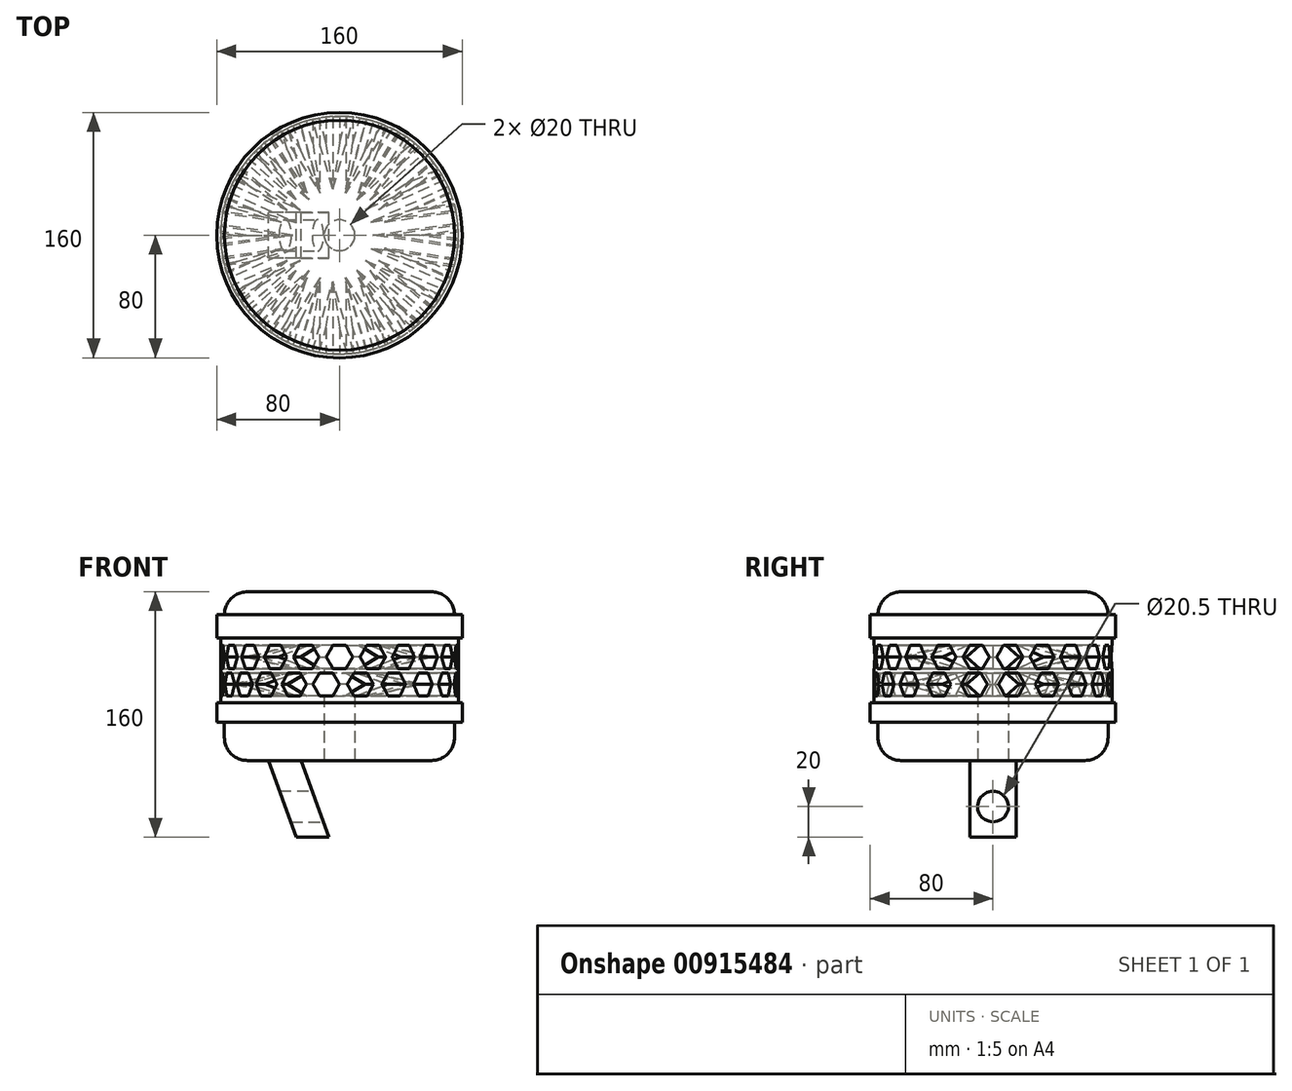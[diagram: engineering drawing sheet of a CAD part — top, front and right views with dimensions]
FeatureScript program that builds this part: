
annotation { "Feature Type Name" : "Feature", "Feature Type Description" : "" }
export const myFeature = defineFeature(function(context is Context, id is Id, definition is map)
    precondition{}
    {
        {
            var Q0;
            Q0=qCreatedBy(makeId("Top.planeOp"),FACE);
            var sketch = newSketch(context, id + "F0", { "sketchPlane" : qUnion([Q0])});
            skCircle(sketch, "E0", {"center": v(0, 0) * mm, "radius": 75 * mm});
            skCircle(sketch, "E1", {"center": v(0, 0) * mm, "radius": 80 * mm});
            skCircle(sketch, "E2", {"center": v(0, 0) * mm, "radius": 77.5 * mm});
            skSolve(sketch);
        }
        {
            var Q0;
            Q0=makeQuery(id+"F0.imprint","IMPRINT",FACE,{"disambiguationData":[TD([[makeQuery(id+"F0.imprint","IMPRINT",EDGE,{"derivedFrom":sQuery(id+"F0.wireOp",EDGE,"E0")}),1.0]])]});
            extrude(context, id + "F1", {"entities" : qUnion([Q0]), "depth" : 110 * mm, "offsetDistance" : 25 * mm});
        }
        {
            var Q0;
            Q0=makeQuery(id+"F1.opExtrude","CAP_EDGE",EDGE,{"disambiguationData":[OSD([sQuery(id+"F0.wireOp",EDGE,"E0")])],"isStart":false});
            var Q1;
            Q1=makeQuery(id+"F1.opExtrude","CAP_EDGE",EDGE,{"disambiguationData":[OSD([sQuery(id+"F0.wireOp",EDGE,"E0")])],"isStart":true});
            fillet(context, id + "F2", {"entities" : qUnion([Q0, Q1]), "radius" : 15 * mm, "tangentPropagation" : true, "allowEdgeOverflow" : false});
        }
        {
            var Q0;
            Q0=makeQuery(id+"F0.imprint","IMPRINT",FACE,{"disambiguationData":[TD([[makeQuery(id+"F0.imprint","IMPRINT",EDGE,{"derivedFrom":sQuery(id+"F0.wireOp",EDGE,"E0")}),-1.0]])]});
            var Q1;
            Q1=makeQuery(id+"F0.imprint","IMPRINT",FACE,{"disambiguationData":[TD([[makeQuery(id+"F0.imprint","IMPRINT",EDGE,{"derivedFrom":sQuery(id+"F0.wireOp",EDGE,"E1")}),1.0]])]});
            extrude(context, id + "F3", {"entities" : qUnion([Q0, Q1]), "operationType" : NewBodyOperationType.ADD, "depth" : 95 * mm, "offsetDistance" : 25 * mm});
        }
        {
            var Q0;
            Q0=makeQuery(id+"F0.imprint","IMPRINT",FACE,{"disambiguationData":[TD([[makeQuery(id+"F0.imprint","IMPRINT",EDGE,{"derivedFrom":sQuery(id+"F0.wireOp",EDGE,"E1")}),1.0]])]});
            extrude(context, id + "F4", {"entities" : qUnion([Q0]), "operationType" : NewBodyOperationType.REMOVE, "depth" : 80 * mm, "offsetDistance" : 25 * mm});
        }
        {
            var Q0;
            Q0=makeQuery(id+"F0.imprint","IMPRINT",FACE,{"disambiguationData":[TD([[makeQuery(id+"F0.imprint","IMPRINT",EDGE,{"derivedFrom":sQuery(id+"F0.wireOp",EDGE,"E1")}),1.0]])]});
            extrude(context, id + "F5", {"entities" : qUnion([Q0]), "operationType" : NewBodyOperationType.ADD, "depth" : 37.5 * mm, "offsetDistance" : 25 * mm});
        }
        {
            var Q0;
            Q0=makeQuery(id+"F0.imprint","IMPRINT",FACE,{"disambiguationData":[TD([[makeQuery(id+"F0.imprint","IMPRINT",EDGE,{"derivedFrom":sQuery(id+"F0.wireOp",EDGE,"E1")}),1.0]])]});
            var Q1;
            Q1=makeQuery(id+"F0.imprint","IMPRINT",FACE,{"disambiguationData":[TD([[makeQuery(id+"F0.imprint","IMPRINT",EDGE,{"derivedFrom":sQuery(id+"F0.wireOp",EDGE,"E0")}),-1.0]])]});
            extrude(context, id + "F6", {"entities" : qUnion([Q0, Q1]), "operationType" : NewBodyOperationType.REMOVE, "depth" : 25 * mm, "offsetDistance" : 25 * mm});
        }
        {
            var Q0;
            Q0=qCreatedBy(makeId("Front.planeOp"),FACE);
            var sketch = newSketch(context, id + "F7", { "sketchPlane" : qUnion([Q0])});
            skCircle(sketch, "E3.cCircle", {"center": v(0, 67.5) * mm, "radius": 8.66 * mm, "construction": true});
            skLineSegment(sketch, "E3.0", {"start": v(4.33, 75) * mm, "end": v(8.66, 67.5) * mm});
            skLineSegment(sketch, "E3.1", {"start": v(8.66, 67.5) * mm, "end": v(4.33, 60) * mm});
            skLineSegment(sketch, "E3.2", {"start": v(4.33, 60) * mm, "end": v(-4.33, 60) * mm});
            skLineSegment(sketch, "E3.3", {"start": v(-4.33, 60) * mm, "end": v(-8.66, 67.5) * mm});
            skLineSegment(sketch, "E3.4", {"start": v(-8.66, 67.5) * mm, "end": v(-4.33, 75) * mm});
            skLineSegment(sketch, "E3.5", {"start": v(-4.33, 75) * mm, "end": v(4.33, 75) * mm});
            skLineSegment(sketch, "E4", {"start": v(0, 67.5) * mm, "end": v(-8.66, 67.5) * mm});
            skLineSegment(sketch, "E5", {"start": v(-8.66, 67.5) * mm, "end": v(-8.66, 49.65) * mm});
            skCircle(sketch, "E6.cCircle", {"center": v(-8.66, 49.65) * mm, "radius": 8.66 * mm, "construction": true});
            skLineSegment(sketch, "E6.0", {"start": v(-13, 57.15) * mm, "end": v(-4.33, 57.15) * mm});
            skLineSegment(sketch, "E6.1", {"start": v(-4.33, 57.15) * mm, "end": v(0, 49.65) * mm});
            skLineSegment(sketch, "E6.2", {"start": v(0, 49.65) * mm, "end": v(-4.33, 42.15) * mm});
            skLineSegment(sketch, "E6.3", {"start": v(-4.33, 42.15) * mm, "end": v(-13, 42.15) * mm});
            skLineSegment(sketch, "E6.4", {"start": v(-13, 42.15) * mm, "end": v(-17.32, 49.65) * mm});
            skLineSegment(sketch, "E6.5", {"start": v(-17.32, 49.65) * mm, "end": v(-13, 57.15) * mm});
            skSolve(sketch);
        }
        {
            var Q0;
            Q0=makeQuery(id+"F7.imprint","IMPRINT",FACE,{"disambiguationData":[TD([[makeQuery(id+"F7.imprint","IMPRINT",EDGE,{"derivedFrom":sQuery(id+"F7.wireOp",EDGE,"E3.0")}),-1.0]])]});
            var Q1;
            {var subQ0=sQuery(id+"F7.wireOp",EDGE,"E6.1");Q1=makeQuery(id+"F7.imprint","IMPRINT",FACE,{"disambiguationData":[TD([[makeQuery(id+"F7.imprint","IMPRINT",EDGE,{"derivedFrom":subQ0}),-1.0]])]});}
            extrude(context, id + "F8", {"entities" : qUnion([Q0, Q1]), "oppositeDirection" : true, "depth" : 120 * mm, "offsetDistance" : 25 * mm, "hasSecondDirection" : true, "secondDirectionOppositeDirection" : false, "secondDirectionDepth" : 120 * mm});
        }
        {
            var Q0;
            Q0=qCreatedBy(makeId("Right.planeOp"),FACE);
            var sketch = newSketch(context, id + "F9", { "sketchPlane" : qUnion([Q0])});
            skLineSegment(sketch, "E7", {"start": v(0, 0) * mm, "end": v(0, 75) * mm});
            skSolve(sketch);
        }
        {
            var Q0;
            Q0=makeQuery(id+"F8.opExtrude","SWEPT_BODY",BODY,{"disambiguationData":[OSD([sQuery(id+"F7.wireOp",EDGE,"E3.0"),sQuery(id+"F7.wireOp",EDGE,"E3.1"),sQuery(id+"F7.wireOp",EDGE,"E3.2"),sQuery(id+"F7.wireOp",EDGE,"E3.3"),sQuery(id+"F7.wireOp",EDGE,"E3.4"),sQuery(id+"F7.wireOp",EDGE,"E3.5")])]});
            var Q1;
            Q1=sQuery(id+"F9.wireOp",EDGE,"E7");
            circularPattern(context, id + "F10", {"entities" : qUnion([Q0]), "axis" : qUnion([Q1]), "angle" : 360 * degree, "instanceCount" : 11, "equalSpace" : true});
        }
        {
            var Q0;
            Q0=qCreatedBy(makeId("Front.planeOp"),FACE);
            var sketch = newSketch(context, id + "F11", { "sketchPlane" : qUnion([Q0])});
            skLineSegment(sketch, "E8", {"start": v(-8.66, 0) * mm, "end": v(-8.66, 49.45) * mm});
            skSolve(sketch);
        }
        {
            var Q0;
            Q0=makeQuery(id+"F8.opExtrude","SWEPT_BODY",BODY,{"disambiguationData":[OSD([sQuery(id+"F7.wireOp",EDGE,"E6.0"),sQuery(id+"F7.wireOp",EDGE,"E6.1"),sQuery(id+"F7.wireOp",EDGE,"E6.2"),sQuery(id+"F7.wireOp",EDGE,"E6.3"),sQuery(id+"F7.wireOp",EDGE,"E6.4"),sQuery(id+"F7.wireOp",EDGE,"E6.5")])]});
            var Q1;
            Q1=sQuery(id+"F11.wireOp",EDGE,"E8");
            circularPattern(context, id + "F12", {"entities" : qUnion([Q0]), "axis" : qUnion([Q1]), "angle" : 360 * degree, "instanceCount" : 11, "equalSpace" : true});
        }
        {
            var Q0;
            Q0=makeQuery(id+"F8.opExtrude","SWEPT_BODY",BODY,{"disambiguationData":[OSD([sQuery(id+"F7.wireOp",EDGE,"E3.0"),sQuery(id+"F7.wireOp",EDGE,"E3.1"),sQuery(id+"F7.wireOp",EDGE,"E3.2"),sQuery(id+"F7.wireOp",EDGE,"E3.3"),sQuery(id+"F7.wireOp",EDGE,"E3.4"),sQuery(id+"F7.wireOp",EDGE,"E3.5")])]});
            var Q1;
            Q1=makeQuery(id+"F10.opPattern","COPY",BODY,{"derivedFrom":makeQuery(id+"F8.opExtrude","SWEPT_BODY",BODY,{"disambiguationData":[OSD([sQuery(id+"F7.wireOp",EDGE,"E3.0"),sQuery(id+"F7.wireOp",EDGE,"E3.1"),sQuery(id+"F7.wireOp",EDGE,"E3.2"),sQuery(id+"F7.wireOp",EDGE,"E3.3"),sQuery(id+"F7.wireOp",EDGE,"E3.4"),sQuery(id+"F7.wireOp",EDGE,"E3.5")])]}),"instanceName":"5"});
            var Q2;
            Q2=makeQuery(id+"F10.opPattern","COPY",BODY,{"derivedFrom":makeQuery(id+"F8.opExtrude","SWEPT_BODY",BODY,{"disambiguationData":[OSD([sQuery(id+"F7.wireOp",EDGE,"E3.0"),sQuery(id+"F7.wireOp",EDGE,"E3.1"),sQuery(id+"F7.wireOp",EDGE,"E3.2"),sQuery(id+"F7.wireOp",EDGE,"E3.3"),sQuery(id+"F7.wireOp",EDGE,"E3.4"),sQuery(id+"F7.wireOp",EDGE,"E3.5")])]}),"instanceName":"6"});
            var Q3;
            Q3=makeQuery(id+"F10.opPattern","COPY",BODY,{"derivedFrom":makeQuery(id+"F8.opExtrude","SWEPT_BODY",BODY,{"disambiguationData":[OSD([sQuery(id+"F7.wireOp",EDGE,"E3.0"),sQuery(id+"F7.wireOp",EDGE,"E3.1"),sQuery(id+"F7.wireOp",EDGE,"E3.2"),sQuery(id+"F7.wireOp",EDGE,"E3.3"),sQuery(id+"F7.wireOp",EDGE,"E3.4"),sQuery(id+"F7.wireOp",EDGE,"E3.5")])]}),"instanceName":"1"});
            var Q4;
            Q4=makeQuery(id+"F10.opPattern","COPY",BODY,{"derivedFrom":makeQuery(id+"F8.opExtrude","SWEPT_BODY",BODY,{"disambiguationData":[OSD([sQuery(id+"F7.wireOp",EDGE,"E3.0"),sQuery(id+"F7.wireOp",EDGE,"E3.1"),sQuery(id+"F7.wireOp",EDGE,"E3.2"),sQuery(id+"F7.wireOp",EDGE,"E3.3"),sQuery(id+"F7.wireOp",EDGE,"E3.4"),sQuery(id+"F7.wireOp",EDGE,"E3.5")])]}),"instanceName":"7"});
            var Q5;
            Q5=makeQuery(id+"F10.opPattern","COPY",BODY,{"derivedFrom":makeQuery(id+"F8.opExtrude","SWEPT_BODY",BODY,{"disambiguationData":[OSD([sQuery(id+"F7.wireOp",EDGE,"E3.0"),sQuery(id+"F7.wireOp",EDGE,"E3.1"),sQuery(id+"F7.wireOp",EDGE,"E3.2"),sQuery(id+"F7.wireOp",EDGE,"E3.3"),sQuery(id+"F7.wireOp",EDGE,"E3.4"),sQuery(id+"F7.wireOp",EDGE,"E3.5")])]}),"instanceName":"2"});
            var Q6;
            Q6=makeQuery(id+"F10.opPattern","COPY",BODY,{"derivedFrom":makeQuery(id+"F8.opExtrude","SWEPT_BODY",BODY,{"disambiguationData":[OSD([sQuery(id+"F7.wireOp",EDGE,"E3.0"),sQuery(id+"F7.wireOp",EDGE,"E3.1"),sQuery(id+"F7.wireOp",EDGE,"E3.2"),sQuery(id+"F7.wireOp",EDGE,"E3.3"),sQuery(id+"F7.wireOp",EDGE,"E3.4"),sQuery(id+"F7.wireOp",EDGE,"E3.5")])]}),"instanceName":"8"});
            var Q7;
            Q7=makeQuery(id+"F10.opPattern","COPY",BODY,{"derivedFrom":makeQuery(id+"F8.opExtrude","SWEPT_BODY",BODY,{"disambiguationData":[OSD([sQuery(id+"F7.wireOp",EDGE,"E3.0"),sQuery(id+"F7.wireOp",EDGE,"E3.1"),sQuery(id+"F7.wireOp",EDGE,"E3.2"),sQuery(id+"F7.wireOp",EDGE,"E3.3"),sQuery(id+"F7.wireOp",EDGE,"E3.4"),sQuery(id+"F7.wireOp",EDGE,"E3.5")])]}),"instanceName":"3"});
            var Q8;
            Q8=makeQuery(id+"F10.opPattern","COPY",BODY,{"derivedFrom":makeQuery(id+"F8.opExtrude","SWEPT_BODY",BODY,{"disambiguationData":[OSD([sQuery(id+"F7.wireOp",EDGE,"E3.0"),sQuery(id+"F7.wireOp",EDGE,"E3.1"),sQuery(id+"F7.wireOp",EDGE,"E3.2"),sQuery(id+"F7.wireOp",EDGE,"E3.3"),sQuery(id+"F7.wireOp",EDGE,"E3.4"),sQuery(id+"F7.wireOp",EDGE,"E3.5")])]}),"instanceName":"9"});
            var Q9;
            Q9=makeQuery(id+"F10.opPattern","COPY",BODY,{"derivedFrom":makeQuery(id+"F8.opExtrude","SWEPT_BODY",BODY,{"disambiguationData":[OSD([sQuery(id+"F7.wireOp",EDGE,"E3.0"),sQuery(id+"F7.wireOp",EDGE,"E3.1"),sQuery(id+"F7.wireOp",EDGE,"E3.2"),sQuery(id+"F7.wireOp",EDGE,"E3.3"),sQuery(id+"F7.wireOp",EDGE,"E3.4"),sQuery(id+"F7.wireOp",EDGE,"E3.5")])]}),"instanceName":"4"});
            var Q10;
            Q10=makeQuery(id+"F10.opPattern","COPY",BODY,{"derivedFrom":makeQuery(id+"F8.opExtrude","SWEPT_BODY",BODY,{"disambiguationData":[OSD([sQuery(id+"F7.wireOp",EDGE,"E3.0"),sQuery(id+"F7.wireOp",EDGE,"E3.1"),sQuery(id+"F7.wireOp",EDGE,"E3.2"),sQuery(id+"F7.wireOp",EDGE,"E3.3"),sQuery(id+"F7.wireOp",EDGE,"E3.4"),sQuery(id+"F7.wireOp",EDGE,"E3.5")])]}),"instanceName":"10"});
            var Q11;
            Q11=makeQuery(id+"F12.opPattern","COPY",BODY,{"derivedFrom":makeQuery(id+"F8.opExtrude","SWEPT_BODY",BODY,{"disambiguationData":[OSD([sQuery(id+"F7.wireOp",EDGE,"E6.0"),sQuery(id+"F7.wireOp",EDGE,"E6.1"),sQuery(id+"F7.wireOp",EDGE,"E6.2"),sQuery(id+"F7.wireOp",EDGE,"E6.3"),sQuery(id+"F7.wireOp",EDGE,"E6.4"),sQuery(id+"F7.wireOp",EDGE,"E6.5")])]}),"instanceName":"6"});
            var Q12;
            Q12=makeQuery(id+"F12.opPattern","COPY",BODY,{"derivedFrom":makeQuery(id+"F8.opExtrude","SWEPT_BODY",BODY,{"disambiguationData":[OSD([sQuery(id+"F7.wireOp",EDGE,"E6.0"),sQuery(id+"F7.wireOp",EDGE,"E6.1"),sQuery(id+"F7.wireOp",EDGE,"E6.2"),sQuery(id+"F7.wireOp",EDGE,"E6.3"),sQuery(id+"F7.wireOp",EDGE,"E6.4"),sQuery(id+"F7.wireOp",EDGE,"E6.5")])]}),"instanceName":"1"});
            var Q13;
            Q13=makeQuery(id+"F12.opPattern","COPY",BODY,{"derivedFrom":makeQuery(id+"F8.opExtrude","SWEPT_BODY",BODY,{"disambiguationData":[OSD([sQuery(id+"F7.wireOp",EDGE,"E6.0"),sQuery(id+"F7.wireOp",EDGE,"E6.1"),sQuery(id+"F7.wireOp",EDGE,"E6.2"),sQuery(id+"F7.wireOp",EDGE,"E6.3"),sQuery(id+"F7.wireOp",EDGE,"E6.4"),sQuery(id+"F7.wireOp",EDGE,"E6.5")])]}),"instanceName":"5"});
            var Q14;
            Q14=makeQuery(id+"F12.opPattern","COPY",BODY,{"derivedFrom":makeQuery(id+"F8.opExtrude","SWEPT_BODY",BODY,{"disambiguationData":[OSD([sQuery(id+"F7.wireOp",EDGE,"E6.0"),sQuery(id+"F7.wireOp",EDGE,"E6.1"),sQuery(id+"F7.wireOp",EDGE,"E6.2"),sQuery(id+"F7.wireOp",EDGE,"E6.3"),sQuery(id+"F7.wireOp",EDGE,"E6.4"),sQuery(id+"F7.wireOp",EDGE,"E6.5")])]}),"instanceName":"10"});
            var Q15;
            Q15=makeQuery(id+"F12.opPattern","COPY",BODY,{"derivedFrom":makeQuery(id+"F8.opExtrude","SWEPT_BODY",BODY,{"disambiguationData":[OSD([sQuery(id+"F7.wireOp",EDGE,"E6.0"),sQuery(id+"F7.wireOp",EDGE,"E6.1"),sQuery(id+"F7.wireOp",EDGE,"E6.2"),sQuery(id+"F7.wireOp",EDGE,"E6.3"),sQuery(id+"F7.wireOp",EDGE,"E6.4"),sQuery(id+"F7.wireOp",EDGE,"E6.5")])]}),"instanceName":"4"});
            var Q16;
            Q16=makeQuery(id+"F12.opPattern","COPY",BODY,{"derivedFrom":makeQuery(id+"F8.opExtrude","SWEPT_BODY",BODY,{"disambiguationData":[OSD([sQuery(id+"F7.wireOp",EDGE,"E6.0"),sQuery(id+"F7.wireOp",EDGE,"E6.1"),sQuery(id+"F7.wireOp",EDGE,"E6.2"),sQuery(id+"F7.wireOp",EDGE,"E6.3"),sQuery(id+"F7.wireOp",EDGE,"E6.4"),sQuery(id+"F7.wireOp",EDGE,"E6.5")])]}),"instanceName":"9"});
            var Q17;
            Q17=makeQuery(id+"F12.opPattern","COPY",BODY,{"derivedFrom":makeQuery(id+"F8.opExtrude","SWEPT_BODY",BODY,{"disambiguationData":[OSD([sQuery(id+"F7.wireOp",EDGE,"E6.0"),sQuery(id+"F7.wireOp",EDGE,"E6.1"),sQuery(id+"F7.wireOp",EDGE,"E6.2"),sQuery(id+"F7.wireOp",EDGE,"E6.3"),sQuery(id+"F7.wireOp",EDGE,"E6.4"),sQuery(id+"F7.wireOp",EDGE,"E6.5")])]}),"instanceName":"3"});
            var Q18;
            Q18=makeQuery(id+"F12.opPattern","COPY",BODY,{"derivedFrom":makeQuery(id+"F8.opExtrude","SWEPT_BODY",BODY,{"disambiguationData":[OSD([sQuery(id+"F7.wireOp",EDGE,"E6.0"),sQuery(id+"F7.wireOp",EDGE,"E6.1"),sQuery(id+"F7.wireOp",EDGE,"E6.2"),sQuery(id+"F7.wireOp",EDGE,"E6.3"),sQuery(id+"F7.wireOp",EDGE,"E6.4"),sQuery(id+"F7.wireOp",EDGE,"E6.5")])]}),"instanceName":"8"});
            var Q19;
            Q19=makeQuery(id+"F12.opPattern","COPY",BODY,{"derivedFrom":makeQuery(id+"F8.opExtrude","SWEPT_BODY",BODY,{"disambiguationData":[OSD([sQuery(id+"F7.wireOp",EDGE,"E6.0"),sQuery(id+"F7.wireOp",EDGE,"E6.1"),sQuery(id+"F7.wireOp",EDGE,"E6.2"),sQuery(id+"F7.wireOp",EDGE,"E6.3"),sQuery(id+"F7.wireOp",EDGE,"E6.4"),sQuery(id+"F7.wireOp",EDGE,"E6.5")])]}),"instanceName":"2"});
            var Q20;
            Q20=makeQuery(id+"F12.opPattern","COPY",BODY,{"derivedFrom":makeQuery(id+"F8.opExtrude","SWEPT_BODY",BODY,{"disambiguationData":[OSD([sQuery(id+"F7.wireOp",EDGE,"E6.0"),sQuery(id+"F7.wireOp",EDGE,"E6.1"),sQuery(id+"F7.wireOp",EDGE,"E6.2"),sQuery(id+"F7.wireOp",EDGE,"E6.3"),sQuery(id+"F7.wireOp",EDGE,"E6.4"),sQuery(id+"F7.wireOp",EDGE,"E6.5")])]}),"instanceName":"7"});
            var Q21;
            Q21=makeQuery(id+"F8.opExtrude","SWEPT_BODY",BODY,{"disambiguationData":[OSD([sQuery(id+"F7.wireOp",EDGE,"E6.0"),sQuery(id+"F7.wireOp",EDGE,"E6.1"),sQuery(id+"F7.wireOp",EDGE,"E6.2"),sQuery(id+"F7.wireOp",EDGE,"E6.3"),sQuery(id+"F7.wireOp",EDGE,"E6.4"),sQuery(id+"F7.wireOp",EDGE,"E6.5")])]});
            var Q22;
            Q22=makeQuery(id+"F1.opExtrude","SWEPT_BODY",BODY,{"disambiguationData":[OSD([sQuery(id+"F0.wireOp",EDGE,"E0")])]});
            booleanBodies(context, id + "F13", {"operationType" : BooleanOperationType.SUBTRACTION, "tools" : qUnion([Q0, Q1, Q2, Q3, Q4, Q5, Q6, Q7, Q8, Q9, Q10, Q11, Q12, Q13, Q14, Q15, Q16, Q17, Q18, Q19, Q20, Q21]), "targets" : qUnion([Q22])});
        }
        {
            var Q0;
            Q0=makeQuery(id+"F0.imprint","IMPRINT",FACE,{"disambiguationData":[TD([[makeQuery(id+"F0.imprint","IMPRINT",EDGE,{"derivedFrom":sQuery(id+"F0.wireOp",EDGE,"E0")}),1.0]])]});
            var sketch = newSketch(context, id + "F14", { "sketchPlane" : qUnion([Q0])});
            skCircle(sketch, "E9", {"center": v(0, 0) * mm, "radius": 10 * mm});
            skSolve(sketch);
        }
        {
            var Q0;
            Q0=makeQuery(id+"F14.imprint","IMPRINT",FACE,{"disambiguationData":[TD([[makeQuery(id+"F14.imprint","IMPRINT",EDGE,{"derivedFrom":sQuery(id+"F14.wireOp",EDGE,"E9")}),1.0]])]});
            extrude(context, id + "F15", {"entities" : qUnion([Q0]), "operationType" : NewBodyOperationType.REMOVE, "depth" : 61.6 * mm, "offsetDistance" : 25 * mm});
        }
        {
            var Q0;
            Q0=qCreatedBy(makeId("Front.planeOp"),FACE);
            var sketch = newSketch(context, id + "F16", { "sketchPlane" : qUnion([Q0])});
            skLineSegment(sketch, "E10", {"start": v(0, 0) * mm, "end": v(0, -50) * mm});
            skLineSegment(sketch, "E11", {"start": v(0, -50) * mm, "end": v(-25, -50) * mm});
            skLineSegment(sketch, "E12", {"start": v(-25, -50) * mm, "end": v(-25, 0) * mm});
            skLineSegment(sketch, "E13", {"start": v(-25, 0) * mm, "end": v(-6.8, -50) * mm});
            skLineSegment(sketch, "E14", {"start": v(-28.09, -50) * mm, "end": v(-46.28, 0) * mm});
            skLineSegment(sketch, "E15", {"start": v(-6.8, -50) * mm, "end": v(-28.09, -50) * mm});
            skLineSegment(sketch, "E16", {"start": v(-25, 0) * mm, "end": v(-46.28, 0) * mm});
            skSolve(sketch);
        }
        {
            var Q0;
            Q0=makeQuery(id+"F16.imprint","IMPRINT",FACE,{"disambiguationData":[TD([[makeQuery(id+"F16.imprint","IMPRINT",EDGE,{"derivedFrom":sQuery(id+"F16.wireOp",EDGE,"E13")}),-1.0]])]});
            var Q1;
            {var subQ0=sQuery(id+"F16.wireOp",EDGE,"E12");Q1=makeQuery(id+"F16.imprint","IMPRINT",FACE,{"disambiguationData":[TD([[makeQuery(id+"F16.imprint","IMPRINT",EDGE,{"derivedFrom":subQ0}),1.0]])]});}
            extrude(context, id + "F17", {"entities" : qUnion([Q0, Q1]), "operationType" : NewBodyOperationType.ADD, "depth" : 15 * mm, "offsetDistance" : 25 * mm, "hasSecondDirection" : true, "secondDirectionOppositeDirection" : true, "secondDirectionDepth" : 15 * mm});
        }
        {
            var Q0;
            Q0=qCreatedBy(makeId("Right.planeOp"),FACE);
            var sketch = newSketch(context, id + "F18", { "sketchPlane" : qUnion([Q0])});
            skCircle(sketch, "E17", {"center": v(0, -30) * mm, "radius": 10.25 * mm});
            skSolve(sketch);
        }
        {
            var Q0;
            Q0=makeQuery(id+"F18.imprint","IMPRINT",FACE,{"disambiguationData":[TD([[makeQuery(id+"F18.imprint","IMPRINT",EDGE,{"derivedFrom":sQuery(id+"F18.wireOp",EDGE,"E17")}),1.0]])]});
            extrude(context, id + "F19", {"entities" : qUnion([Q0]), "operationType" : NewBodyOperationType.REMOVE, "oppositeDirection" : true, "depth" : 110.6 * mm, "offsetDistance" : 25 * mm});
        }
    });
